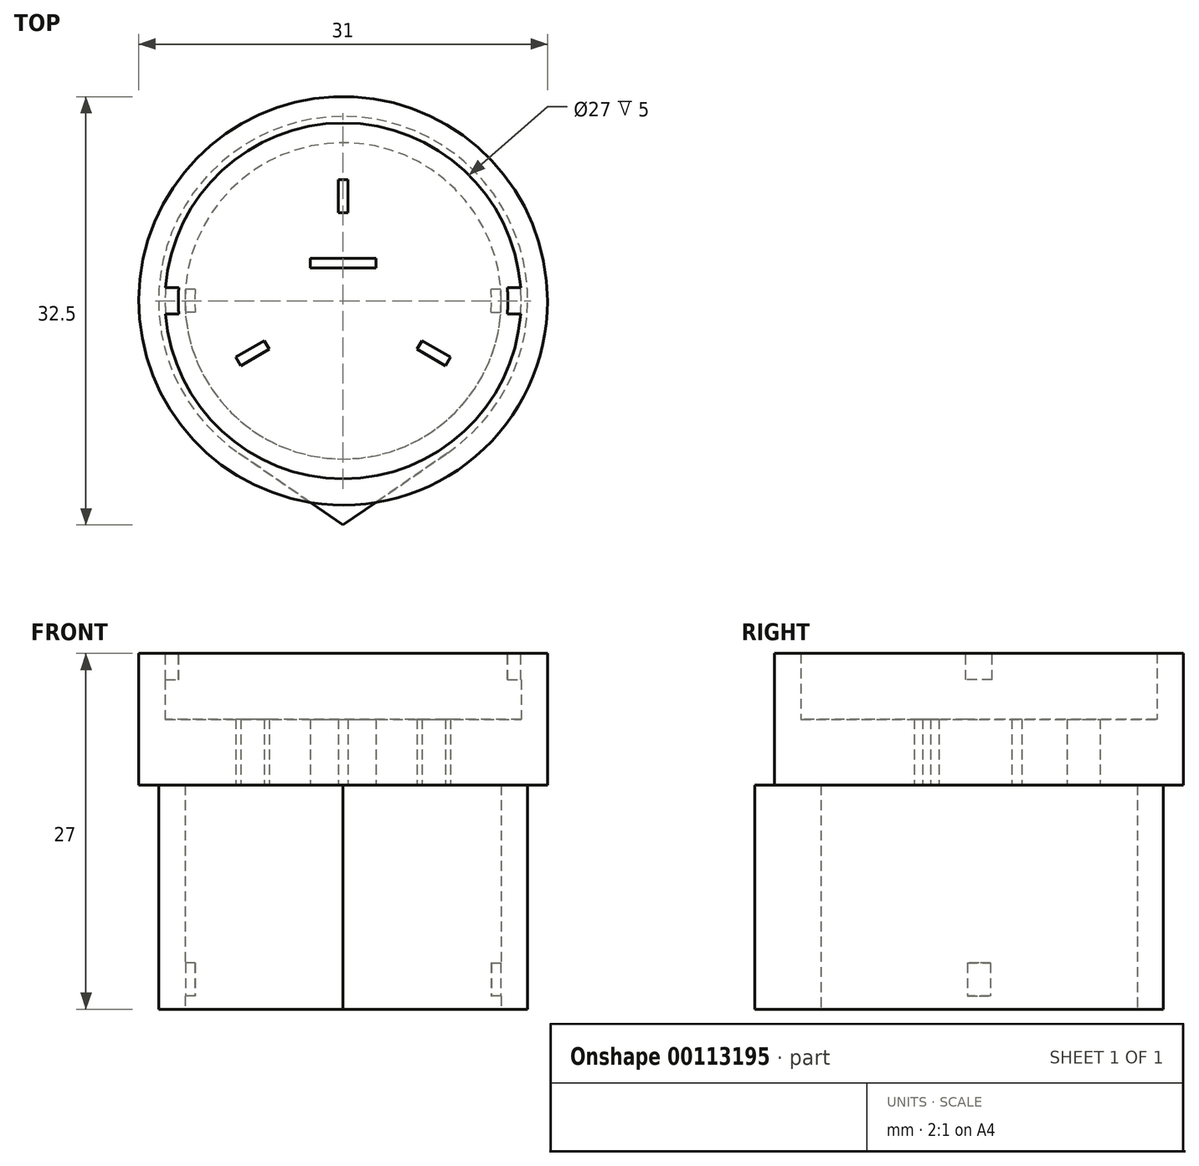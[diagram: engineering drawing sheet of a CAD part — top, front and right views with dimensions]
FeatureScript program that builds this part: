
annotation { "Feature Type Name" : "Feature", "Feature Type Description" : "" }
export const myFeature = defineFeature(function(context is Context, id is Id, definition is map)
    precondition{}
    {
        {
            var Q0;
            Q0=qCreatedBy(makeId("Top.planeOp"),FACE);
            var sketch = newSketch(context, id + "F0", { "sketchPlane" : qUnion([Q0])});
            skCircle(sketch, "E0", {"center": v(0, 0) * mm, "radius": 12 * mm});
            skCircle(sketch, "E1.0", {"center": v(0, 0) * mm, "radius": 14 * mm});
            skSolve(sketch);
        }
        {
            var Q0;
            Q0=makeQuery(id+"F0.imprint","IMPRINT",FACE,{"disambiguationData":[TD([[makeQuery(id+"F0.imprint","IMPRINT",EDGE,{"derivedFrom":sQuery(id+"F0.wireOp",EDGE,"E0")}),-1.0]])]});
            extrude(context, id + "F1", {"entities" : qUnion([Q0]), "depth" : 16 * mm});
        }
        {
            var Q0;
            Q0=qCreatedBy(makeId("Top.planeOp"),FACE);
            var sketch = newSketch(context, id + "F2", { "sketchPlane" : qUnion([Q0])});
            skLineSegment(sketch, "E2", {"start": v(12, 0) * mm, "end": v(-12, 0) * mm, "construction": true});
            skArc(sketch, "E3.0", {"start": v(-11.97, 0.87) * mm, "mid": v(-12, 0) * mm, "end": v(-11.97, -0.87) * mm});
            skLineSegment(sketch, "E4", {"start": v(11.97, 0.88) * mm, "end": v(11.22, 0.88) * mm});
            skLineSegment(sketch, "E5", {"start": v(11.22, -0.88) * mm, "end": v(11.97, -0.88) * mm});
            skArc(sketch, "E6", {"start": v(-11.22, 0.87) * mm, "mid": v(-11.25, 0) * mm, "end": v(-11.22, -0.87) * mm});
            skLineSegment(sketch, "E7", {"start": v(-11.22, 0.88) * mm, "end": v(-11.97, 0.88) * mm});
            skLineSegment(sketch, "E8", {"start": v(-11.22, -0.88) * mm, "end": v(-11.97, -0.88) * mm});
            skLineSegment(sketch, "E9", {"start": v(11.6, 0.87) * mm, "end": v(11.6, -0.88) * mm, "construction": true});
            skPoint(sketch, "E10", {"position": v(11.6, 0) * mm});
            skArc(sketch, "E11.trimOffspring", {"start": v(11.97, -0.87) * mm, "mid": v(12, 0) * mm, "end": v(11.97, 0.87) * mm});
            skArc(sketch, "E12.trimOffspring", {"start": v(11.22, -0.87) * mm, "mid": v(11.25, 0) * mm, "end": v(11.22, 0.88) * mm});
            skSolve(sketch);
        }
        {
            var Q0;
            Q0=qSketchRegion(id+"F2",true);
            extrude(context, id + "F3", {"entities" : qUnion([Q0]), "operationType" : NewBodyOperationType.ADD, "depth" : 2.5 * mm});
        }
        {
            var Q0;
            Q0=makeQuery(id+"F1.opExtrude","CAP_FACE",FACE,{"disambiguationData":[OSD([sQuery(id+"F0.wireOp",EDGE,"E0"),sQuery(id+"F0.wireOp",EDGE,"E1.0")])],"isStart":false});
            var sketch = newSketch(context, id + "F4", { "sketchPlane" : qUnion([Q0])});
            skCircle(sketch, "E13", {"center": v(0, 0) * mm, "radius": 15.5 * mm});
            skSolve(sketch);
        }
        {
            var Q0;
            Q0=qSketchRegion(id+"F4",true);
            extrude(context, id + "F5", {"entities" : qUnion([Q0]), "operationType" : NewBodyOperationType.ADD, "depth" : 5 * mm});
        }
        {
            var Q0;
            Q0=makeQuery(id+"F5.boolean.opBoolean","SPLIT",FACE,{"disambiguationData":[TD([makeQuery(id+"F1.opExtrude","SWEPT_FACE",FACE,{"disambiguationData":[OSD([sQuery(id+"F0.wireOp",EDGE,"E0")])]})])],"derivedFrom":makeQuery(id+"F5.opExtrude","CAP_FACE",FACE,{"disambiguationData":[OSD([sQuery(id+"F4.wireOp",EDGE,"E13")])],"isStart":true})});
            var sketch = newSketch(context, id + "F6", { "sketchPlane" : qUnion([Q0])});
            skLineSegment(sketch, "E14", {"start": v(0, 0) * mm, "end": v(0, -12) * mm, "construction": true});
            skCircle(sketch, "E15", {"center": v(0, 0) * mm, "radius": 4.92 * mm, "construction": true});
            skCircle(sketch, "E16", {"center": v(0, 0) * mm, "radius": 9.53 * mm, "construction": true});
            skCircle(sketch, "E17", {"center": v(0, 0) * mm, "radius": 6.35 * mm, "construction": true});
            skLineSegment(sketch, "E18.bottom", {"start": v(2.5, -2.49) * mm, "end": v(-2.5, -2.49) * mm});
            skLineSegment(sketch, "E18.top", {"start": v(2.5, -3.24) * mm, "end": v(-2.5, -3.24) * mm});
            skLineSegment(sketch, "E18.left", {"start": v(2.5, -2.49) * mm, "end": v(2.5, -3.24) * mm});
            skLineSegment(sketch, "E18.right", {"start": v(-2.5, -2.49) * mm, "end": v(-2.5, -3.24) * mm});
            skPoint(sketch, "E18.middle", {"position": v(0, -2.86) * mm});
            skLineSegment(sketch, "E19.bottom", {"start": v(0.38, -9.19) * mm, "end": v(-0.37, -9.19) * mm});
            skLineSegment(sketch, "E19.top", {"start": v(0.38, -6.69) * mm, "end": v(-0.37, -6.69) * mm});
            skLineSegment(sketch, "E19.left", {"start": v(0.37, -9.19) * mm, "end": v(0.37, -6.69) * mm});
            skLineSegment(sketch, "E19.right", {"start": v(-0.38, -9.19) * mm, "end": v(-0.38, -6.69) * mm});
            skPoint(sketch, "E19.middle", {"position": v(0, -7.94) * mm});
            skLineSegment(sketch, "E20", {"start": v(0, -6.35) * mm, "end": v(0, -9.53) * mm});
            skLineSegment(sketch, "E21.1.0", {"start": v(5.5, 3.17) * mm, "end": v(8.25, 4.76) * mm});
            skLineSegment(sketch, "E21.1.1", {"start": v(8.14, 4.27) * mm, "end": v(5.98, 3.02) * mm});
            skLineSegment(sketch, "E21.1.2", {"start": v(7.77, 4.92) * mm, "end": v(5.6, 3.67) * mm});
            skLineSegment(sketch, "E21.1.3", {"start": v(5.6, 3.67) * mm, "end": v(5.98, 3.02) * mm});
            skPoint(sketch, "E21.1.4", {"position": v(6.87, 3.97) * mm});
            skLineSegment(sketch, "E21.1.5", {"start": v(7.77, 4.92) * mm, "end": v(8.14, 4.27) * mm});
            skLineSegment(sketch, "E21.2.0", {"start": v(-5.5, 3.17) * mm, "end": v(-8.25, 4.76) * mm});
            skLineSegment(sketch, "E21.2.1", {"start": v(-7.77, 4.92) * mm, "end": v(-5.6, 3.67) * mm});
            skLineSegment(sketch, "E21.2.2", {"start": v(-8.14, 4.27) * mm, "end": v(-5.98, 3.02) * mm});
            skLineSegment(sketch, "E21.2.3", {"start": v(-5.98, 3.02) * mm, "end": v(-5.6, 3.67) * mm});
            skPoint(sketch, "E21.2.4", {"position": v(-6.87, 3.97) * mm});
            skLineSegment(sketch, "E21.2.5", {"start": v(-8.14, 4.27) * mm, "end": v(-7.77, 4.92) * mm});
            skSolve(sketch);
        }
        {
            var Q0;
            Q0=qSketchRegion(id+"F6",true);
            extrude(context, id + "F7", {"entities" : qUnion([Q0]), "operationType" : NewBodyOperationType.REMOVE, "endBound" : BoundingType.THROUGH_ALL, "oppositeDirection" : true, "depth" : 25 * mm});
        }
        {
            var Q0;
            Q0=makeQuery(id+"F5.opExtrude","CAP_FACE",FACE,{"disambiguationData":[OSD([sQuery(id+"F4.wireOp",EDGE,"E13")])],"isStart":false});
            var sketch = newSketch(context, id + "F8", { "sketchPlane" : qUnion([Q0])});
            skCircle(sketch, "E22.0", {"center": v(0, 0) * mm, "radius": 15.5 * mm});
            skCircle(sketch, "E23.0", {"center": v(0, 0) * mm, "radius": 13.5 * mm});
            skSolve(sketch);
        }
        {
            var Q0;
            Q0=makeQuery(id+"F8.imprint","IMPRINT",FACE,{"disambiguationData":[TD([[makeQuery(id+"F8.imprint","IMPRINT",EDGE,{"derivedFrom":sQuery(id+"F8.wireOp",EDGE,"E22.0")}),1.0]])]});
            extrude(context, id + "F9", {"entities" : qUnion([Q0]), "operationType" : NewBodyOperationType.ADD, "depth" : 5 * mm});
        }
        {
            var Q0;
            Q0=makeQuery(id+"F9.opExtrude","CAP_FACE",FACE,{"disambiguationData":[OSD([sQuery(id+"F8.wireOp",EDGE,"E22.0"),sQuery(id+"F8.wireOp",EDGE,"E23.0")])],"isStart":false});
            var sketch = newSketch(context, id + "F10", { "sketchPlane" : qUnion([Q0])});
            skLineSegment(sketch, "E24.bottom", {"start": v(-13.46, 1) * mm, "end": v(-12.46, 1) * mm});
            skLineSegment(sketch, "E24.top", {"start": v(-13.46, -1) * mm, "end": v(-12.46, -1) * mm});
            skLineSegment(sketch, "E24.left", {"start": v(-13.46, 1) * mm, "end": v(-13.46, -1) * mm, "construction": true});
            skLineSegment(sketch, "E24.right", {"start": v(13.46, 1) * mm, "end": v(13.46, -1) * mm, "construction": true});
            skPoint(sketch, "E24.middle", {"position": v(0, 0) * mm});
            skLineSegment(sketch, "E25", {"start": v(-12.46, 1) * mm, "end": v(12.46, 1) * mm, "construction": true});
            skLineSegment(sketch, "E26", {"start": v(12.46, 1) * mm, "end": v(13.46, 1) * mm});
            skArc(sketch, "E27", {"start": v(12.46, 1) * mm, "mid": v(0, 12.5) * mm, "end": v(-12.46, 1) * mm, "construction": true});
            skArc(sketch, "E28", {"start": v(-12.46, 1) * mm, "mid": v(-12.5, 0) * mm, "end": v(-12.46, -1) * mm});
            skArc(sketch, "E29", {"start": v(-12.46, -1) * mm, "mid": v(0, -12.5) * mm, "end": v(12.46, -1) * mm, "construction": true});
            skArc(sketch, "E30", {"start": v(12.46, -1) * mm, "mid": v(12.5, 0) * mm, "end": v(12.46, 1) * mm});
            skLineSegment(sketch, "E31", {"start": v(12.46, -1) * mm, "end": v(13.46, -1) * mm});
            skLineSegment(sketch, "E32", {"start": v(-12.46, -1) * mm, "end": v(12.46, -1) * mm, "construction": true});
            skArc(sketch, "E33", {"start": v(-13.46, 1) * mm, "mid": v(-13.5, 0) * mm, "end": v(-13.46, -1) * mm});
            skArc(sketch, "E34", {"start": v(-13.46, -1) * mm, "mid": v(0, -13.5) * mm, "end": v(13.46, -1) * mm, "construction": true});
            skArc(sketch, "E35", {"start": v(13.46, 1) * mm, "mid": v(0, 13.5) * mm, "end": v(-13.46, 1) * mm, "construction": true});
            skArc(sketch, "E36", {"start": v(13.46, -1) * mm, "mid": v(13.5, 0) * mm, "end": v(13.46, 1) * mm});
            skSolve(sketch);
        }
        {
            var Q0;
            Q0 = qSketchRegion(id + "F10", true);
            extrude(context, id + "F11", {"entities" : qUnion([Q0]), "operationType" : NewBodyOperationType.ADD, "oppositeDirection" : true, "depth" : 2 * mm});
        }
        {
            var Q0;
            {var subQ0=sQuery(id+"F4.wireOp",EDGE,"E13");Q0=makeQuery(id+"F5.boolean.opBoolean","SPLIT",FACE,{"disambiguationData":[TD([makeQuery(id+"F1.opExtrude","SWEPT_FACE",FACE,{"disambiguationData":[OSD([sQuery(id+"F0.wireOp",EDGE,"E1.0")])]})])],"derivedFrom":makeQuery(id+"F5.opExtrude","CAP_FACE",FACE,{"disambiguationData":[OSD([subQ0])],"isStart":true})});}
            var sketch = newSketch(context, id + "F12", { "sketchPlane" : qUnion([Q0])});
            skArc(sketch, "E37.0", {"start": v(7.94, 11.53) * mm, "mid": v(0, 14) * mm, "end": v(-7.94, 11.53) * mm});
            skLineSegment(sketch, "E38", {"start": v(0, 0) * mm, "end": v(0, 17) * mm, "construction": true});
            skLineSegment(sketch, "E39", {"start": v(0, 17) * mm, "end": v(-7.94, 11.53) * mm});
            skLineSegment(sketch, "E40", {"start": v(0, 17) * mm, "end": v(7.94, 11.53) * mm});
            skSolve(sketch);
        }
        {
            var Q0;
            Q0 = qSketchRegion(id + "F12", true);
            var Q1;
            Q1=makeQuery(id+"F3.boolean.opBoolean","MERGE",FACE,{"derivedFrom":[makeQuery(id+"F1.opExtrude","CAP_FACE",FACE,{"disambiguationData":[OSD([sQuery(id+"F0.wireOp",EDGE,"E0"),sQuery(id+"F0.wireOp",EDGE,"E1.0")])],"isStart":true}),makeQuery(id+"F3.opExtrude","CAP_FACE",FACE,{"disambiguationData":[OSD([sQuery(id+"F2.wireOp",EDGE,"E3.0"),sQuery(id+"F2.wireOp",EDGE,"E6"),sQuery(id+"F2.wireOp",EDGE,"E7"),sQuery(id+"F2.wireOp",EDGE,"E8")])],"isStart":true}),makeQuery(id+"F3.opExtrude","CAP_FACE",FACE,{"disambiguationData":[OSD([sQuery(id+"F2.wireOp",EDGE,"E4"),sQuery(id+"F2.wireOp",EDGE,"E5"),sQuery(id+"F2.wireOp",EDGE,"E11.trimOffspring"),sQuery(id+"F2.wireOp",EDGE,"E12.trimOffspring")])],"isStart":true})]});
            extrude(context, id + "F13", {"entities" : qUnion([Q0]), "operationType" : NewBodyOperationType.ADD, "endBound" : BoundingType.UP_TO_SURFACE, "endBoundEntityFace" : qUnion([Q1]), "depth" : 25 * mm});
        }
        {
            var Q0;
            {var subQ0=sQuery(id+"F2.wireOp",EDGE,"E12.trimOffspring");var subQ1=sQuery(id+"F2.wireOp",EDGE,"E11.trimOffspring");var subQ2=sQuery(id+"F2.wireOp",EDGE,"E8");var subQ3=sQuery(id+"F2.wireOp",EDGE,"E7");var subQ4=sQuery(id+"F2.wireOp",EDGE,"E6");var subQ5=sQuery(id+"F2.wireOp",EDGE,"E5");var subQ6=sQuery(id+"F2.wireOp",EDGE,"E4");var subQ7=sQuery(id+"F2.wireOp",EDGE,"E3.0");var subQ8=sQuery(id+"F0.wireOp",EDGE,"E1.0");var subQ9=sQuery(id+"F0.wireOp",EDGE,"E0");Q0=makeQuery(id+"F13.boolean.opBoolean","MERGE",FACE,{"derivedFrom":[makeQuery(id+"F3.boolean.opBoolean","MERGE",FACE,{"derivedFrom":[makeQuery(id+"F1.opExtrude","CAP_FACE",FACE,{"disambiguationData":[OSD([subQ9,subQ8])],"isStart":true}),makeQuery(id+"F3.opExtrude","CAP_FACE",FACE,{"disambiguationData":[OSD([subQ7,subQ4,subQ3,subQ2])],"isStart":true}),makeQuery(id+"F3.opExtrude","CAP_FACE",FACE,{"disambiguationData":[OSD([subQ6,subQ5,subQ1,subQ0])],"isStart":true})]}),makeQuery(id+"F13.opExtrude","CAP_FACE",FACE,{"disambiguationData":[OSD([subQ9,subQ8,subQ7,subQ6,subQ5,subQ4,subQ3,subQ2,subQ1,subQ0])],"isStart":false})]});}
            var sketch = newSketch(context, id + "F14", { "sketchPlane" : qUnion([Q0])});
            skArc(sketch, "E41.0", {"start": v(7.94, 11.53) * mm, "mid": v(0, -14) * mm, "end": v(-7.94, 11.53) * mm});
            skLineSegment(sketch, "E41.1", {"start": v(7.94, 11.53) * mm, "end": v(0, 17) * mm});
            skLineSegment(sketch, "E41.2", {"start": v(-7.94, 11.53) * mm, "end": v(0, 17) * mm});
            skCircle(sketch, "E42", {"center": v(0, 0) * mm, "radius": 12 * mm});
            skSolve(sketch);
        }
        {
            var Q0;
            Q0=makeQuery(id+"F14.imprint","IMPRINT",FACE,{"disambiguationData":[TD([[makeQuery(id+"F14.imprint","IMPRINT",EDGE,{"derivedFrom":sQuery(id+"F14.wireOp",EDGE,"E41.0")}),-1.0]])]});
            extrude(context, id + "F15", {"entities" : qUnion([Q0]), "operationType" : NewBodyOperationType.ADD, "depth" : 1 * mm});
        }
    });
